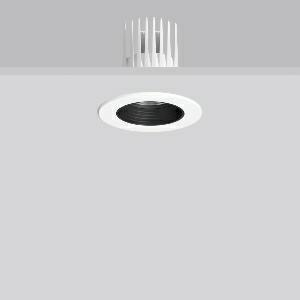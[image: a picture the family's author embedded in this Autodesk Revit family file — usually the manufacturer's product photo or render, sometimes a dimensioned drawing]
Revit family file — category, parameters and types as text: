
# Revit family: heledon_mini_e_901754_002_2_5c63
name_source: partatom
category: Lighting Fixtures
units: mm (PartAtom-declared; Revit-internal decimal feet)

## family parameters
Cut with Voids When Loaded = No
Host = Face
Light Source = No
Part Type = Normal
Room Calculation Point = No
Round Connector Dimension = Use Diameter
Shared = No

## types (1)
- HELEDON mini E (1 x LED Modul 927, 3050 lm, 2700)
    Apparent Load = 29 VA
    Approval mark = CE
    CIE Flux Codes = 80 99 100 100 100
    Color Rendering = 92
    Color Temperature = 2700
    Default Elevation = 1800 mm
    Description = Series: HELEDON mini
Round recessed downlight. Housing: die-cast aluminium, powder-coated. Black plastic ring and recessed LED to prevent glare from the side. Optical assembly with lens made of plastic (polycarbonate) for the best homogeneous light distribution - can be changed without tools. Best colour rendering index Ra>90. Suitable for Recessed ceiling mounting. Installation without tools thanks to spring fastening system. Including separate LED converter with connecting cable 600 mm.High quality converter without flickering and stroboscopic effect. Through-wiring box (5 pole) available as accessory. The following accessories can be mounted without use of tools: interchangeable lenses, decorative glasses, honeycomb louvre, clear and frosted diffusers, white interchangeable plastic ring. 
Colour: traffic white, matt (RAL 9016)
Diameter: 124 mm
Height: 3 mm
Cut-out diameter: 114 mm
Recess height: 170 mm
Luminaire: recess height: 120 mm
Lamp: LED
Socket: without socket
Colour temperature: 2700K
Colour rendering index (CRI): 92
System power: 29 W
Rated luminous flux: 3050 lm
Luminous efficiency: 105 lm/W
Control gear: Regulated power supply
Protection class: II
Type of protection: IP 20
    Height = 0 mm  [stored 0 ft]
    Lamp = 1 x LED Modul 927
    Lamp Light Flux = 3050 lm
    Lamp count = 1
    Length = 124 mm  [stored 0.406824 ft]
    Lifetime = 50000 h
    Luminous efficacy = 105 lm/W
    Manufacturer = RZB
    ModVariant = No
    Model = 901754.002.2
    Mounting Place = Ceiling
    Mounting Type = Recessed
    Number of Poles = 1
    OnlyDefault = Yes
    Power Factor = 1
    Product Name = HELEDON mini E
    Product group = Recessed downlights
    ProductGroupID = 402
    Protection Class = Protection class II
    Protection Degree = IP 20
    RLX_Detail_Level = 1
    RLX_Emergency_Light_Flux = 0 lm
    RLX_Emergency_Type = 0
    RLX_Emergency_Type_DB = No
    RlxData = <blob elided: 124673 chars, md5=7e8d90a1>
    Socket = socket
    Standby Power = 0 W
    System Light Flux = 3050 lm
    System Power = 29 W
    Type Comments = Product without accessories
    Type Image = 901656.002.jpg
    URL = http://relux.com
    VarID = ---
    Voltage = 230 V
    Voltage Range = 220-240 V
    Weight = 0.00 kg
    Width = 0 mm  [stored 0 ft]

note: [stored X ft] marks values corroborated as IEEE doubles in the binary element streams (Revit-internal decimal feet)

## geometry (parser evidence)
native form markers: Blend x4, Sweep x11
no freeform markers — native parametric forms only
